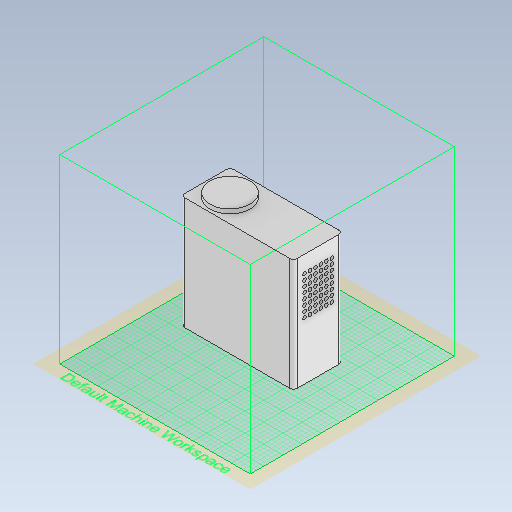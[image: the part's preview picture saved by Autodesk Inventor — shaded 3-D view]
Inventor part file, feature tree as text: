
AUTODESK INVENTOR PART (.ipt)
format: ipt  version: 2021.1 (Build 251245010, 245A)  size: 985,600 bytes
history: native  units: in
note: dims shown in document units (in); Inventor stores cm internally (conversion verified against a paired STEP export)
features: other x9, extrude x9, move_body x4, sketch x3, sheet_metal_op x1
ambient origin geometry x8: Origin, YZ Plane, XZ Plane, XY Plane, X Axis, Y Axis, Z Axis, Center Point
bodies: Body1 (feature_tree), Body2 (feature_tree), Body3 (feature_tree), Body4 (feature_tree), Body5 (feature_tree), Body6 (feature_tree)
feature tree (26):
  other  "bottom"
  sheet_metal_op  "face"
  extrude  "Extrusion9"  Depth=4.252in
  extrude  "Extrusion10"  Depth=4.1339in
  extrude  "Extrusion11"  Depth=4.7244in
  extrude  "Extrusion12"  Depth=0.9843in
  extrude  "Extrusion13"  Depth=4.7244in
  extrude  "Extrusion14"  Depth=0.315in
  extrude  "Extrusion15"  Depth=0.315in
  extrude  "Extrusion16"  Depth=0.1575in
  extrude  "Extrusion17"  Depth=13.7795in
  move_body  "Move Body1"
  move_body  "Move Body2"
  move_body  "Move Body3"
  move_body  "Move Body4"
  sketch  "Sketch6"  dims[d4=0.9843in d5=4.7244in d6=0.9843in d7=4.7244in d8=0.315in d9=0.315in d10=0.1575in d11=13.7795in d12=0.5906in d13=0.5906in d30=11.811in d31=0.0in d32=4.7244in d33=0.0in d34=4.1339in d35=0.0in d36=9.7638in d37=0.0in d38=0.5487in d39=0.0in d40=0.3612in d41=0.0in d42=11.811in d43=0.0in d45=0.315in d46=3.1496in d48=0.4724in d49=2.3622in d51=0.4724in d54=1.1265in d55=0.0in d57=3.1496in d59=2.3622in d60=0.315in d61=0.4724in d62=0.4724in d63=0.811in d64=0.0in d65=0.0in d66=0.0in d67=-0.3937in d68=0.0in d69=0.0in d70=-0.3937in d71=0.0in d72=0.0in d73=-0.3937in d74=0.0in d75=0.0in d76=-5.5118in d77=2.3622in d79=360.0deg d81=0.1575in d82=0.7874in d84=4.3307in d85=0.7874in d87=4.3307in]
  other  "fans"
  other  "TV-BOX"
  other  "Projector"
  other  "top"
  sketch  "Sketch4"  dims[d0=9.7638in d1=4.252in]
  sketch  "Sketch5"  dims[d2=1.1024in d3=4.1339in]
  other  "Composite1"
  other  "Composite2"
  other  "Srf1"
  other  "Srf2"
